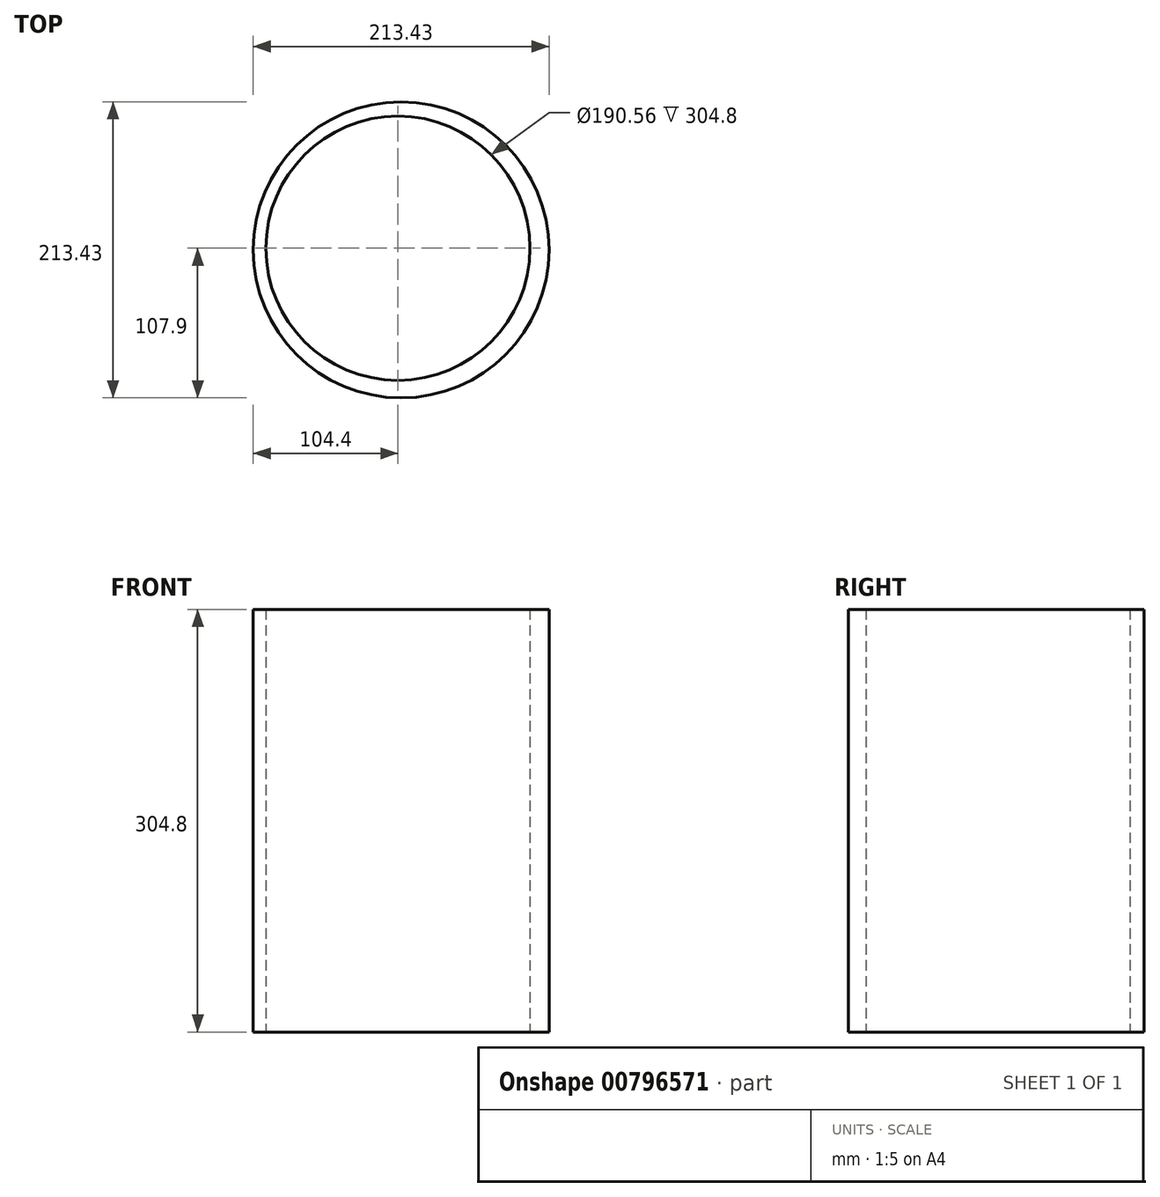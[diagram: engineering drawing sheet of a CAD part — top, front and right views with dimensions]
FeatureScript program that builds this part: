
annotation { "Feature Type Name" : "Feature", "Feature Type Description" : "" }
export const myFeature = defineFeature(function(context is Context, id is Id, definition is map)
    precondition{}
    {
        {
            var Q0;
            Q0=qCreatedBy(makeId("Top.planeOp"),FACE);
            var sketch = newSketch(context, id + "F0", { "sketchPlane" : qUnion([Q0])});
            skCircle(sketch, "E0", {"center": v(2.31, -1.18) * mm, "radius": 106.71 * mm});
            skPoint(sketch, "E0.first.point", {"position": v(-76.34, 70.94) * mm});
            skPoint(sketch, "E0.second.point", {"position": v(78.39, 73.66) * mm});
            skPoint(sketch, "E0.third.point", {"position": v(34.96, -102.78) * mm});
            skSolve(sketch);
        }
        {
            var Q0;
            Q0 = qSketchRegion(id + "F0", true);
            extrude(context, id + "F1", {"entities" : qUnion([Q0]), "endBound" : BoundingType.SYMMETRIC, "depth" : 304.8 * mm, "offsetDistance" : 25.4 * mm});
        }
        {
            var Q0;
            Q0=qCreatedBy(makeId("Top.planeOp"),FACE);
            var sketch = newSketch(context, id + "F2", { "sketchPlane" : qUnion([Q0])});
            skCircle(sketch, "E1", {"center": v(0, 0) * mm, "radius": 95.28 * mm});
            skPoint(sketch, "E1.first.point", {"position": v(-2.48, 95.25) * mm});
            skPoint(sketch, "E1.second.point", {"position": v(86, -41.04) * mm});
            skPoint(sketch, "E1.third.point", {"position": v(-44.45, -84.28) * mm});
            skSolve(sketch);
        }
        {
            var Q0;
            Q0 = qSketchRegion(id + "F2", true);
            extrude(context, id + "F3", {"entities" : qUnion([Q0]), "operationType" : NewBodyOperationType.REMOVE, "endBound" : BoundingType.SYMMETRIC, "depth" : 609.6 * mm, "offsetDistance" : 25.4 * mm});
        }
    });
